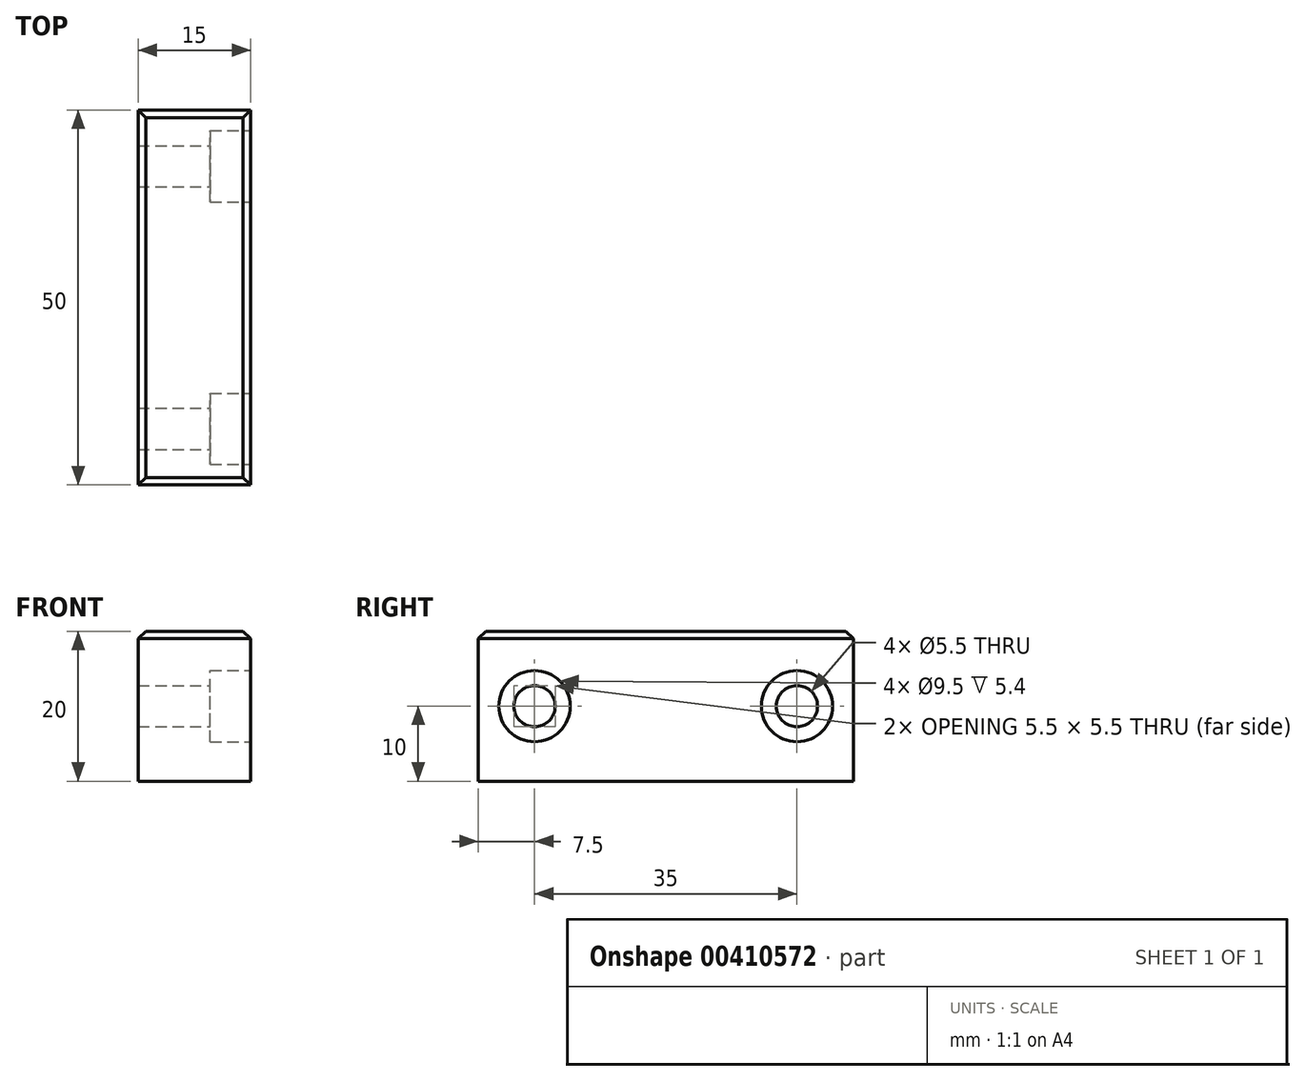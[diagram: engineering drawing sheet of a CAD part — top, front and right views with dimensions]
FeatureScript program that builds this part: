
annotation { "Feature Type Name" : "Feature", "Feature Type Description" : "" }
export const myFeature = defineFeature(function(context is Context, id is Id, definition is map)
    precondition{}
    {
        {
            var Q0;
            Q0=qCreatedBy(makeId("Top.planeOp"),FACE);
            var sketch = newSketch(context, id + "F0", { "sketchPlane" : qUnion([Q0])});
            skLineSegment(sketch, "E0.bottom", {"start": v(0, 0) * mm, "end": v(15, 0) * mm});
            skLineSegment(sketch, "E0.top", {"start": v(0, 50) * mm, "end": v(15, 50) * mm});
            skLineSegment(sketch, "E0.left", {"start": v(0, 0) * mm, "end": v(0, 50) * mm});
            skLineSegment(sketch, "E0.right", {"start": v(15, 0) * mm, "end": v(15, 50) * mm});
            skSolve(sketch);
        }
        {
            var Q0;
            Q0 = qSketchRegion(id + "F0", true);
            extrude(context, id + "F1", {"entities" : qUnion([Q0]), "depth" : 20 * mm});
        }
        {
            var Q0;
            Q0=makeQuery(id+"F1.opExtrude","SWEPT_FACE",FACE,{"disambiguationData":[OSD([sQuery(id+"F0.wireOp",EDGE,"E0.right")])]});
            var sketch = newSketch(context, id + "F2", { "sketchPlane" : qUnion([Q0])});
            skPoint(sketch, "E1", {"position": v(7.5, 10) * mm});
            skPoint(sketch, "E2", {"position": v(42.5, 10) * mm});
            skSolve(sketch);
        }
        {
            var Q0;
            Q0=sQuery(id+"F2.wireOp",VERTEX,"E1");
            var Q1;
            Q1=sQuery(id+"F2.wireOp",VERTEX,"E2");
            var Q2;
            Q2=makeQuery(id+"F1.opExtrude","SWEPT_BODY",BODY,{"disambiguationData":[OSD([sQuery(id+"F0.wireOp",EDGE,"E0.bottom"),sQuery(id+"F0.wireOp",EDGE,"E0.top"),sQuery(id+"F0.wireOp",EDGE,"E0.left"),sQuery(id+"F0.wireOp",EDGE,"E0.right")])]});
            hole(context, id + "F3", {"style" : HoleStyle.C_BORE, "endStyle" : HoleEndStyle.THROUGH, "holeDiameter" : 5.5 * mm, "cBoreDiameter" : 9.5 * mm, "cBoreDepth" : 5.4 * mm, "isTappedThrough" : true, "tappedDepth" : 5.6 * mm, "tapClearance" : 3, "locations" : qUnion([Q0, Q1]), "scope" : qUnion([Q2])});
        }
        {
            var Q0;
            Q0=makeQuery(id+"F1.opExtrude","CAP_EDGE",EDGE,{"disambiguationData":[OSD([sQuery(id+"F0.wireOp",EDGE,"E0.right")])],"isStart":false});
            var Q1;
            Q1=makeQuery(id+"F1.opExtrude","CAP_EDGE",EDGE,{"disambiguationData":[OSD([sQuery(id+"F0.wireOp",EDGE,"E0.bottom")])],"isStart":false});
            var Q2;
            Q2=makeQuery(id+"F1.opExtrude","CAP_EDGE",EDGE,{"disambiguationData":[OSD([sQuery(id+"F0.wireOp",EDGE,"E0.left")])],"isStart":false});
            var Q3;
            Q3=makeQuery(id+"F1.opExtrude","CAP_EDGE",EDGE,{"disambiguationData":[OSD([sQuery(id+"F0.wireOp",EDGE,"E0.top")])],"isStart":false});
            chamfer(context, id + "F4", {"entities" : qUnion([Q0, Q1, Q2, Q3]), "width" : 1 * mm, "tangentPropagation" : true});
        }
    });
